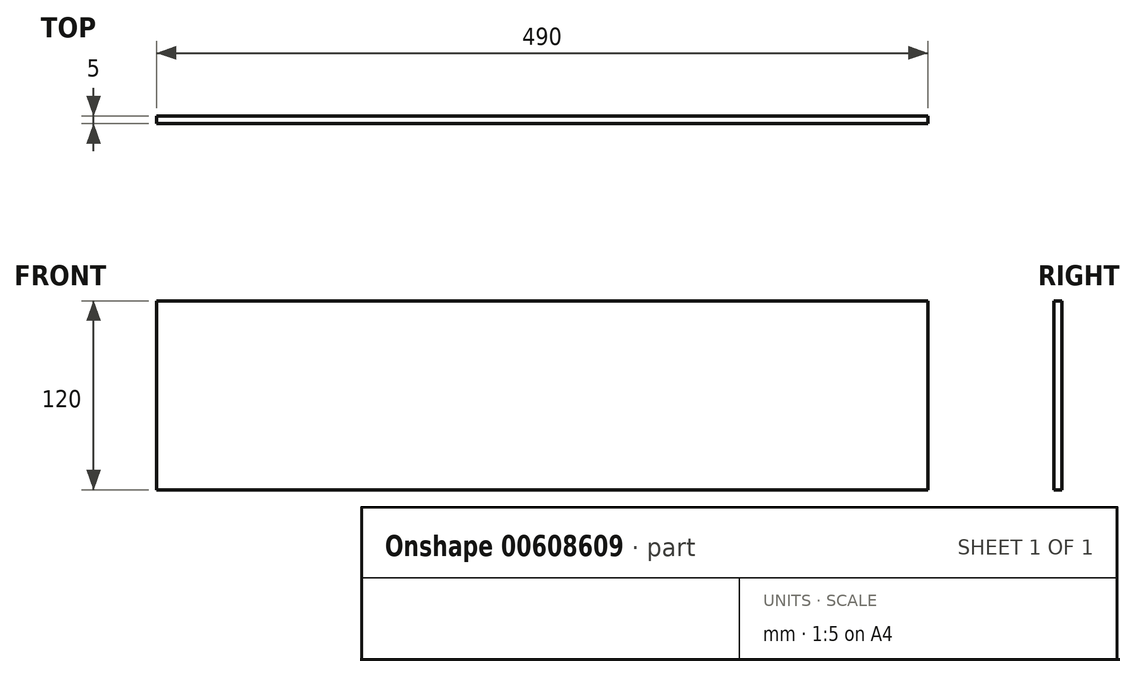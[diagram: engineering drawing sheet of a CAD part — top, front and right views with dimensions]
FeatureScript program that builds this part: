
annotation { "Feature Type Name" : "Feature", "Feature Type Description" : "" }
export const myFeature = defineFeature(function(context is Context, id is Id, definition is map)
    precondition{}
    {
        {
            var Q0;
            Q0=qCreatedBy(makeId("Front.planeOp"),FACE);
            var sketch = newSketch(context, id + "F0", { "sketchPlane" : qUnion([Q0])});
            skLineSegment(sketch, "E0.bottom", {"start": v(0, 0) * mm, "end": v(490, 0) * mm});
            skLineSegment(sketch, "E0.top", {"start": v(0, 120) * mm, "end": v(490, 120) * mm});
            skLineSegment(sketch, "E0.left", {"start": v(0, 0) * mm, "end": v(0, 120) * mm});
            skLineSegment(sketch, "E0.right", {"start": v(490, 0) * mm, "end": v(490, 120) * mm});
            skSolve(sketch);
        }
        {
            var Q0;
            Q0 = qSketchRegion(id + "F0", true);
            extrude(context, id + "F1", {"entities" : qUnion([Q0]), "depth" : 5 * mm, "offsetDistance" : 25 * mm});
        }
    });
